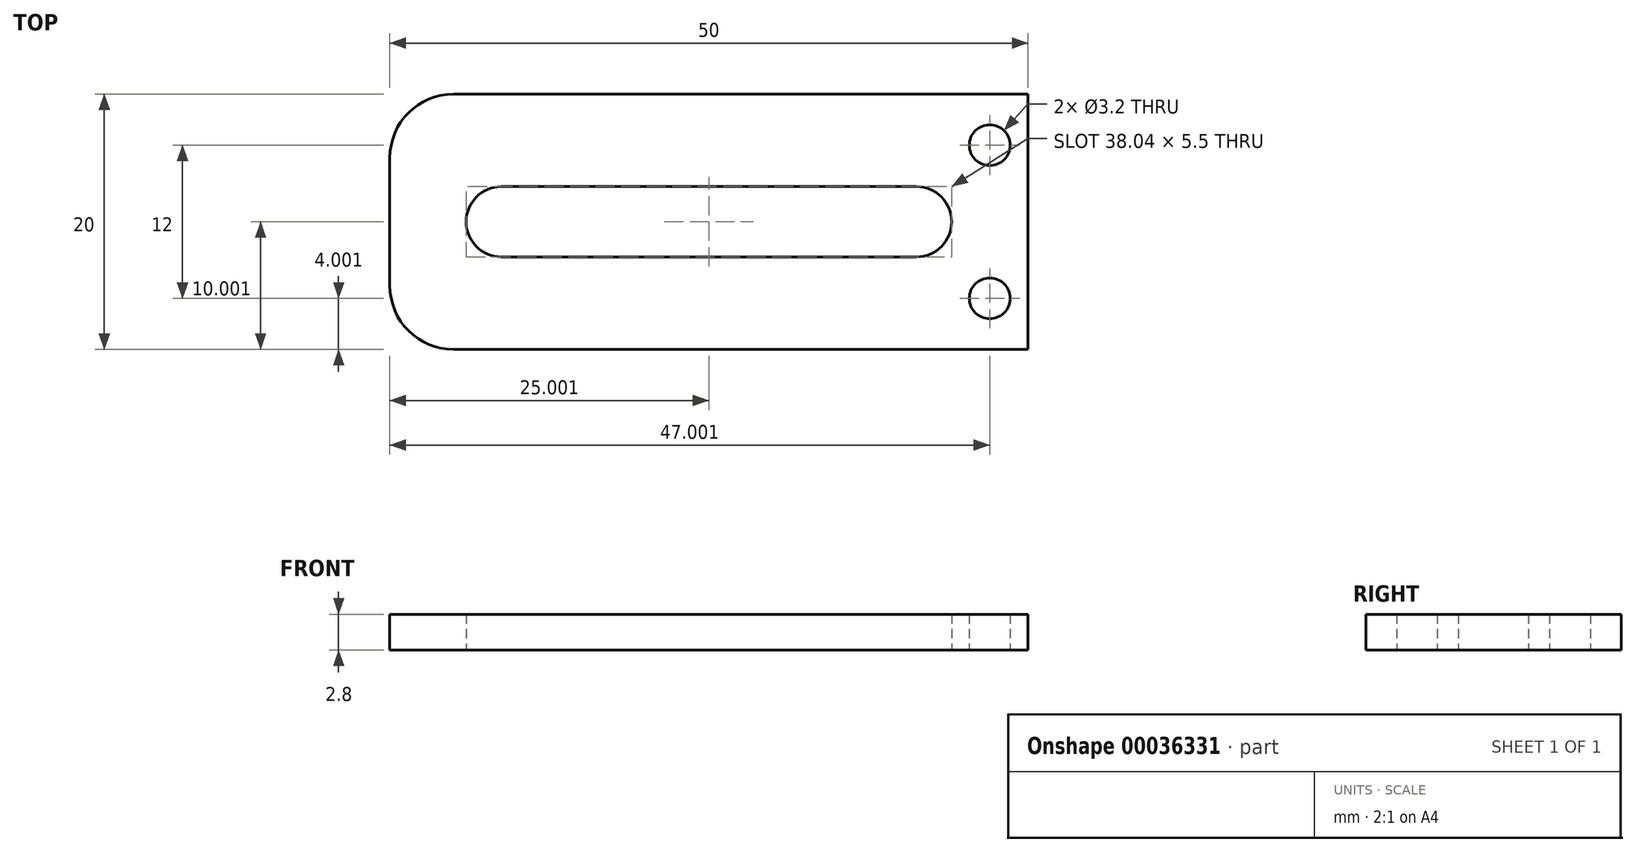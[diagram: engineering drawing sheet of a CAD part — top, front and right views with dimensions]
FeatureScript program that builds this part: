
annotation { "Feature Type Name" : "Feature", "Feature Type Description" : "" }
export const myFeature = defineFeature(function(context is Context, id is Id, definition is map)
    precondition{}
    {
        {
            var Q0;
            Q0=qCreatedBy(makeId("Top.planeOp"),FACE);
            var sketch = newSketch(context, id + "F0", { "sketchPlane" : qUnion([Q0])});
            skLineSegment(sketch, "E0.bottom", {"start": v(28.81, -28.04) * mm, "end": v(-21.19, -28.04) * mm});
            skLineSegment(sketch, "E0.top", {"start": v(28.81, -48.04) * mm, "end": v(-21.19, -48.04) * mm});
            skLineSegment(sketch, "E0.left", {"start": v(28.81, -28.04) * mm, "end": v(28.81, -48.04) * mm});
            skLineSegment(sketch, "E0.right", {"start": v(-21.19, -28.04) * mm, "end": v(-21.19, -48.04) * mm});
            skCircle(sketch, "E1", {"center": v(-12.46, -38.04) * mm, "radius": 2.75 * mm});
            skPoint(sketch, "E1.centerSnap0", {"position": v(-21.19, -38.04) * mm});
            skCircle(sketch, "E2", {"center": v(20.08, -38.04) * mm, "radius": 2.75 * mm});
            skPoint(sketch, "E2.centerSnap0", {"position": v(28.81, -38.04) * mm});
            skLineSegment(sketch, "E3", {"start": v(-21.19, -38.04) * mm, "end": v(-12.46, -38.04) * mm, "construction": true});
            skLineSegment(sketch, "E4", {"start": v(28.81, -38.04) * mm, "end": v(20.08, -38.04) * mm, "construction": true});
            skLineSegment(sketch, "E5.bottom", {"start": v(-12.46, -35.29) * mm, "end": v(20.08, -35.29) * mm});
            skLineSegment(sketch, "E5.top", {"start": v(-12.46, -40.79) * mm, "end": v(20.08, -40.79) * mm});
            skLineSegment(sketch, "E5.left", {"start": v(-12.46, -35.29) * mm, "end": v(-12.46, -40.79) * mm});
            skLineSegment(sketch, "E5.right", {"start": v(20.08, -35.29) * mm, "end": v(20.08, -40.79) * mm});
            skCircle(sketch, "E6", {"center": v(25.81, -44.04) * mm, "radius": 1.6 * mm});
            skCircle(sketch, "E7", {"center": v(25.81, -32.04) * mm, "radius": 1.6 * mm});
            skLineSegment(sketch, "E8", {"start": v(25.81, -32.04) * mm, "end": v(28.81, -32.04) * mm, "construction": true});
            skLineSegment(sketch, "E9", {"start": v(25.81, -44.04) * mm, "end": v(28.81, -44.04) * mm, "construction": true});
            skLineSegment(sketch, "E10", {"start": v(25.81, -32.04) * mm, "end": v(25.81, -28.04) * mm, "construction": true});
            skLineSegment(sketch, "E11", {"start": v(25.81, -44.04) * mm, "end": v(25.81, -48.04) * mm, "construction": true});
            skSolve(sketch);
        }
        {
            var Q0;
            Q0=makeQuery(id+"F0.imprint","IMPRINT",FACE,{"disambiguationData":[TD([[makeQuery(id+"F0.imprint","IMPRINT",EDGE,{"derivedFrom":sQuery(id+"F0.wireOp",EDGE,"E0.bottom")}),1.0]])]});
            extrude(context, id + "F1", {"entities" : qUnion([Q0]), "depth" : 2.8 * mm});
        }
        {
            var Q0;
            Q0=makeQuery(id+"F1.opExtrude","SWEPT_EDGE",EDGE,{"disambiguationData":[OSD([sQuery(id+"F0.wireOp",EDGE,"E0.top"),sQuery(id+"F0.wireOp",EDGE,"E0.right")])]});
            var Q1;
            Q1=makeQuery(id+"F1.opExtrude","SWEPT_EDGE",EDGE,{"disambiguationData":[OSD([sQuery(id+"F0.wireOp",EDGE,"E0.bottom"),sQuery(id+"F0.wireOp",EDGE,"E0.right")])]});
            fillet(context, id + "F2", {"entities" : qUnion([Q0, Q1]), "radius" : 5 * mm, "tangentPropagation" : true, "allowEdgeOverflow" : false});
        }
    });
